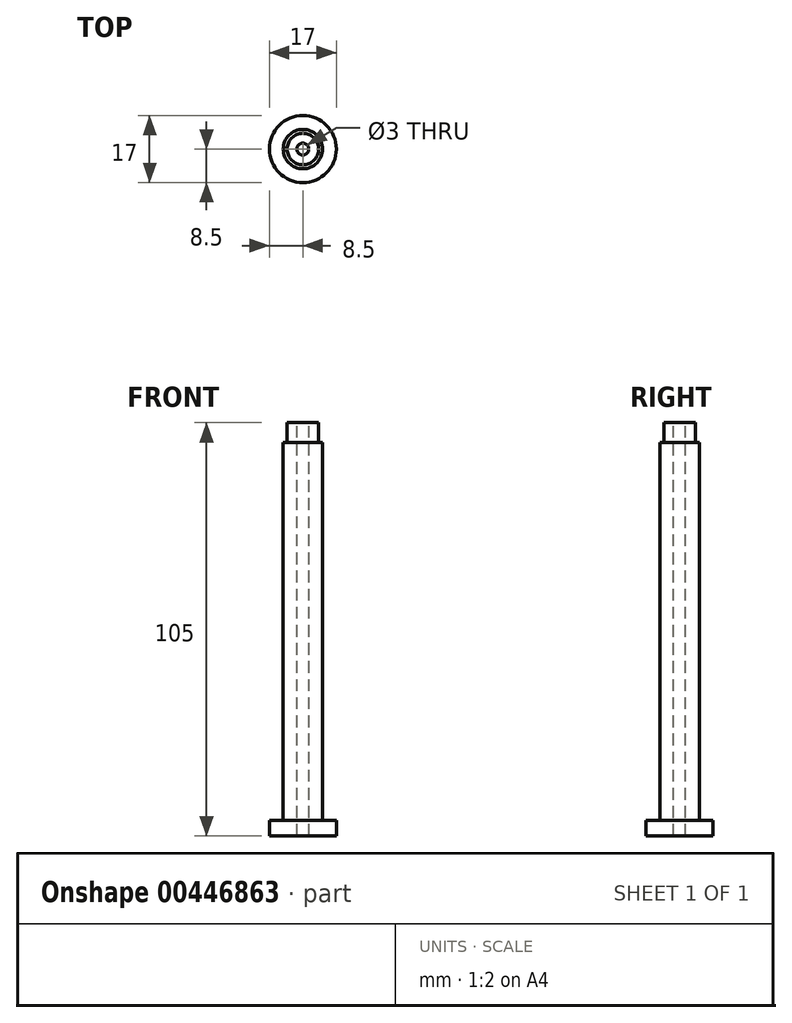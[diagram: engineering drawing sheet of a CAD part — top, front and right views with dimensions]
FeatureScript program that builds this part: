
annotation { "Feature Type Name" : "Feature", "Feature Type Description" : "" }
export const myFeature = defineFeature(function(context is Context, id is Id, definition is map)
    precondition{}
    {
        {
            var Q0;
            Q0=qCreatedBy(makeId("Top.planeOp"),FACE);
            var sketch = newSketch(context, id + "F0", { "sketchPlane" : qUnion([Q0])});
            skCircle(sketch, "E0", {"center": v(0, 0) * mm, "radius": 8.5 * mm});
            skSolve(sketch);
        }
        {
            var Q0;
            Q0=qSketchRegion(id+"F0",true);
            extrude(context, id + "F1", {"entities" : qUnion([Q0]), "depth" : 4 * mm});
        }
        {
            var Q0;
            Q0=qCreatedBy(makeId("Top.planeOp"),FACE);
            var sketch = newSketch(context, id + "F2", { "sketchPlane" : qUnion([Q0])});
            skCircle(sketch, "E1", {"center": v(0, 0) * mm, "radius": 5 * mm});
            skSolve(sketch);
        }
        {
            var Q0;
            Q0=qSketchRegion(id+"F2",true);
            extrude(context, id + "F3", {"entities" : qUnion([Q0]), "operationType" : NewBodyOperationType.ADD, "depth" : 100 * mm});
        }
        {
            var Q0;
            Q0=qCreatedBy(makeId("Right.planeOp"),FACE);
            var sketch = newSketch(context, id + "F4", { "sketchPlane" : qUnion([Q0])});
            skLineSegment(sketch, "E2.bottom", {"start": v(0, 105) * mm, "end": v(4, 105) * mm});
            skLineSegment(sketch, "E2.top", {"start": v(0, 100) * mm, "end": v(4, 100) * mm});
            skLineSegment(sketch, "E2.left", {"start": v(0, 105) * mm, "end": v(0, 100) * mm});
            skLineSegment(sketch, "E2.right", {"start": v(4, 105) * mm, "end": v(4, 100) * mm});
            skSolve(sketch);
        }
        {
            var Q0;
            Q0=makeQuery(id+"F4.imprint","IMPRINT",FACE,{"disambiguationData":[TD([[makeQuery(id+"F4.imprint","IMPRINT",EDGE,{"derivedFrom":sQuery(id+"F4.wireOp",EDGE,"E2.bottom")}),-1.0]])]});
            var Q1;
            Q1=sQuery(id+"F4.wireOp",EDGE,"E2.left");
            revolve(context, id + "F5", {"operationType" : NewBodyOperationType.ADD, "entities" : qUnion([Q0]), "axis" : qUnion([Q1]), "revolveType" : RevolveType.FULL});
        }
        {
            var Q0;
            Q0=makeQuery(id+"F5.opRevolve","SWEPT_FACE",FACE,{"disambiguationData":[OSD([sQuery(id+"F4.wireOp",EDGE,"E2.bottom")])]});
            var sketch = newSketch(context, id + "F6", { "sketchPlane" : qUnion([Q0])});
            skCircle(sketch, "E3", {"center": v(0, 0) * mm, "radius": 1.5 * mm});
            skSolve(sketch);
        }
        {
            var Q0;
            Q0=makeQuery(id+"F6.imprint","IMPRINT",FACE,{"disambiguationData":[TD([[makeQuery(id+"F6.imprint","IMPRINT",EDGE,{"derivedFrom":sQuery(id+"F6.wireOp",EDGE,"E3")}),1.0]])]});
            extrude(context, id + "F7", {"entities" : qUnion([Q0]), "operationType" : NewBodyOperationType.REMOVE, "oppositeDirection" : true, "depth" : 112 * mm});
        }
    });
